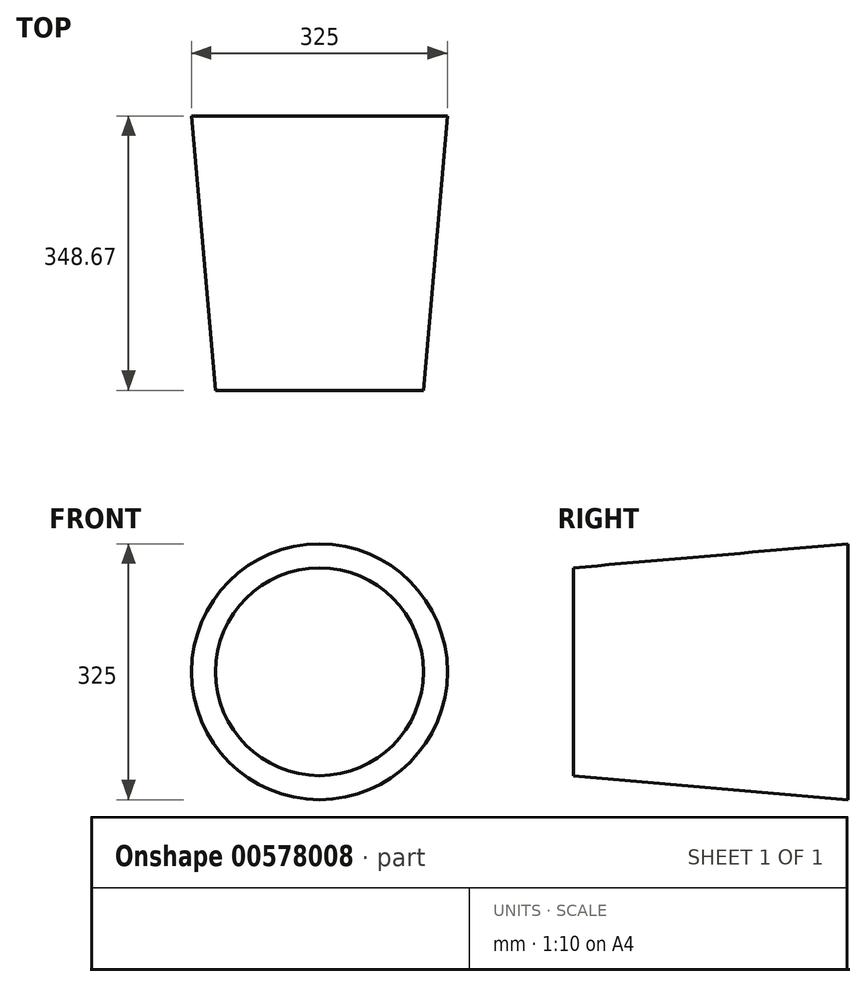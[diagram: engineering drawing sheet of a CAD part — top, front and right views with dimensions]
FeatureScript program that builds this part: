
annotation { "Feature Type Name" : "Feature", "Feature Type Description" : "" }
export const myFeature = defineFeature(function(context is Context, id is Id, definition is map)
    precondition{}
    {
        {
            var Q0;
            Q0=qCreatedBy(makeId("Top.planeOp"),FACE);
            var sketch = newSketch(context, id + "F0", { "sketchPlane" : qUnion([Q0])});
            skLineSegment(sketch, "E0", {"start": v(0, -348.67) * mm, "end": v(132, -348.67) * mm});
            skLineSegment(sketch, "E1", {"start": v(132, -348.67) * mm, "end": v(162.5, 0) * mm});
            skLineSegment(sketch, "E2", {"start": v(162.5, 0) * mm, "end": v(0, 0) * mm});
            skLineSegment(sketch, "E3", {"start": v(0, 0) * mm, "end": v(0, -348.67) * mm});
            skSolve(sketch);
        }
        {
            var Q0;
            Q0=makeQuery(id+"F0.imprint","IMPRINT",FACE,{"disambiguationData":[TD([[makeQuery(id+"F0.imprint","IMPRINT",EDGE,{"derivedFrom":sQuery(id+"F0.wireOp",EDGE,"E0")}),1.0]])]});
            var Q1;
            Q1=sQuery(id+"F0.wireOp",EDGE,"E3");
            revolve(context, id + "F1", {"entities" : qUnion([Q0]), "axis" : qUnion([Q1]), "revolveType" : RevolveType.FULL});
        }
    });
